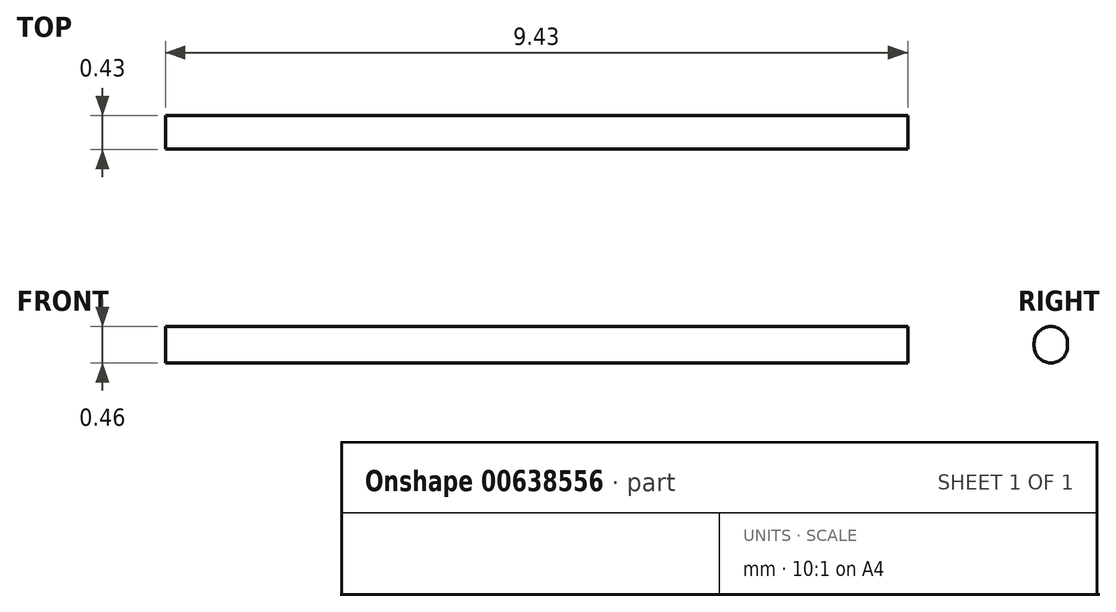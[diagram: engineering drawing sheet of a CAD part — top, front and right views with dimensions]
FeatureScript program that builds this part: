
annotation { "Feature Type Name" : "Feature", "Feature Type Description" : "" }
export const myFeature = defineFeature(function(context is Context, id is Id, definition is map)
    precondition{}
    {
        {
            var Q0;
            Q0=qCreatedBy(makeId("Front.planeOp"),FACE);
            var sketch = newSketch(context, id + "F0", { "sketchPlane" : qUnion([Q0])});
            skLineSegment(sketch, "E0.bottom", {"start": v(-58.69, 3.7) * mm, "end": v(16.73, 3.7) * mm});
            skLineSegment(sketch, "E0.top", {"start": v(-58.69, 0) * mm, "end": v(16.73, 0) * mm});
            skLineSegment(sketch, "E0.left", {"start": v(-58.69, 3.7) * mm, "end": v(-58.69, 0) * mm});
            skLineSegment(sketch, "E0.right", {"start": v(16.73, 3.7) * mm, "end": v(16.73, 0) * mm});
            skLineSegment(sketch, "E1.bottom", {"start": v(16.73, 0) * mm, "end": v(13.34, 0) * mm});
            skLineSegment(sketch, "E1.top", {"start": v(16.73, -5.32) * mm, "end": v(13.34, -5.32) * mm});
            skLineSegment(sketch, "E1.left", {"start": v(16.73, 0) * mm, "end": v(16.73, -5.32) * mm});
            skLineSegment(sketch, "E1.right", {"start": v(13.34, 0) * mm, "end": v(13.34, -5.32) * mm});
            skSolve(sketch);
        }
        {
            var Q0;
            Q0=makeQuery(id+"F0.imprint","IMPRINT",FACE,{"disambiguationData":[TD([[makeQuery(id+"F0.imprint","IMPRINT",EDGE,{"derivedFrom":sQuery(id+"F0.wireOp",EDGE,"E0.bottom")}),-1.0]])]});
            var Q1;
            Q1=makeQuery(id+"F0.imprint","IMPRINT",FACE,{"disambiguationData":[TD([[makeQuery(id+"F0.imprint","IMPRINT",EDGE,{"derivedFrom":sQuery(id+"F0.wireOp",EDGE,"E1.bottom")}),1.0]])]});
            extrude(context, id + "F1", {"entities" : qUnion([Q0, Q1]), "depth" : 3.4 * mm, "offsetDistance" : 25 * mm});
        }
        {
            var Q0;
            Q0=makeQuery(id+"F1.opExtrude","CAP_EDGE",EDGE,{"disambiguationData":[OSD([sQuery(id+"F0.wireOp",EDGE,"E0.bottom")])],"isStart":false});
            var Q1;
            Q1=makeQuery(id+"F1.opExtrude","CAP_EDGE",EDGE,{"disambiguationData":[OSD([sQuery(id+"F0.wireOp",EDGE,"E0.bottom")])],"isStart":true});
            var Q2;
            Q2=makeQuery(id+"F1.opExtrude","CAP_EDGE",EDGE,{"disambiguationData":[OSD([sQuery(id+"F0.wireOp",EDGE,"E0.top")])],"isStart":false});
            var Q3;
            Q3=makeQuery(id+"F1.opExtrude","CAP_EDGE",EDGE,{"disambiguationData":[OSD([sQuery(id+"F0.wireOp",EDGE,"E0.top")])],"isStart":true});
            fillet(context, id + "F2", {"entities" : qUnion([Q0, Q1, Q2, Q3]), "radius" : 1.69 * mm, "tangentPropagation" : true, "allowEdgeOverflow" : false});
        }
        {
            var Q0;
            Q0=makeQuery(id+"F1.opExtrude","SWEPT_BODY",BODY,{"disambiguationData":[OSD([sQuery(id+"F0.wireOp",EDGE,"E0.bottom"),sQuery(id+"F0.wireOp",EDGE,"E0.top"),sQuery(id+"F0.wireOp",EDGE,"E0.left"),sQuery(id+"F0.wireOp",EDGE,"E0.right"),sQuery(id+"F0.wireOp",EDGE,"E1.top"),sQuery(id+"F0.wireOp",EDGE,"E1.left"),sQuery(id+"F0.wireOp",EDGE,"E1.right")])]});
            var Q1;
            Q1=qCreatedBy(makeId("Origin.pointOp"),VERTEX);
            transform(context, id + "F3", {"entities" : qUnion([Q0]), "transformType" : TransformType.SCALE_UNIFORMLY, "scale" : 0.12, "scalePoint" : qUnion([Q1]), "makeCopy" : false});
        }
    });
